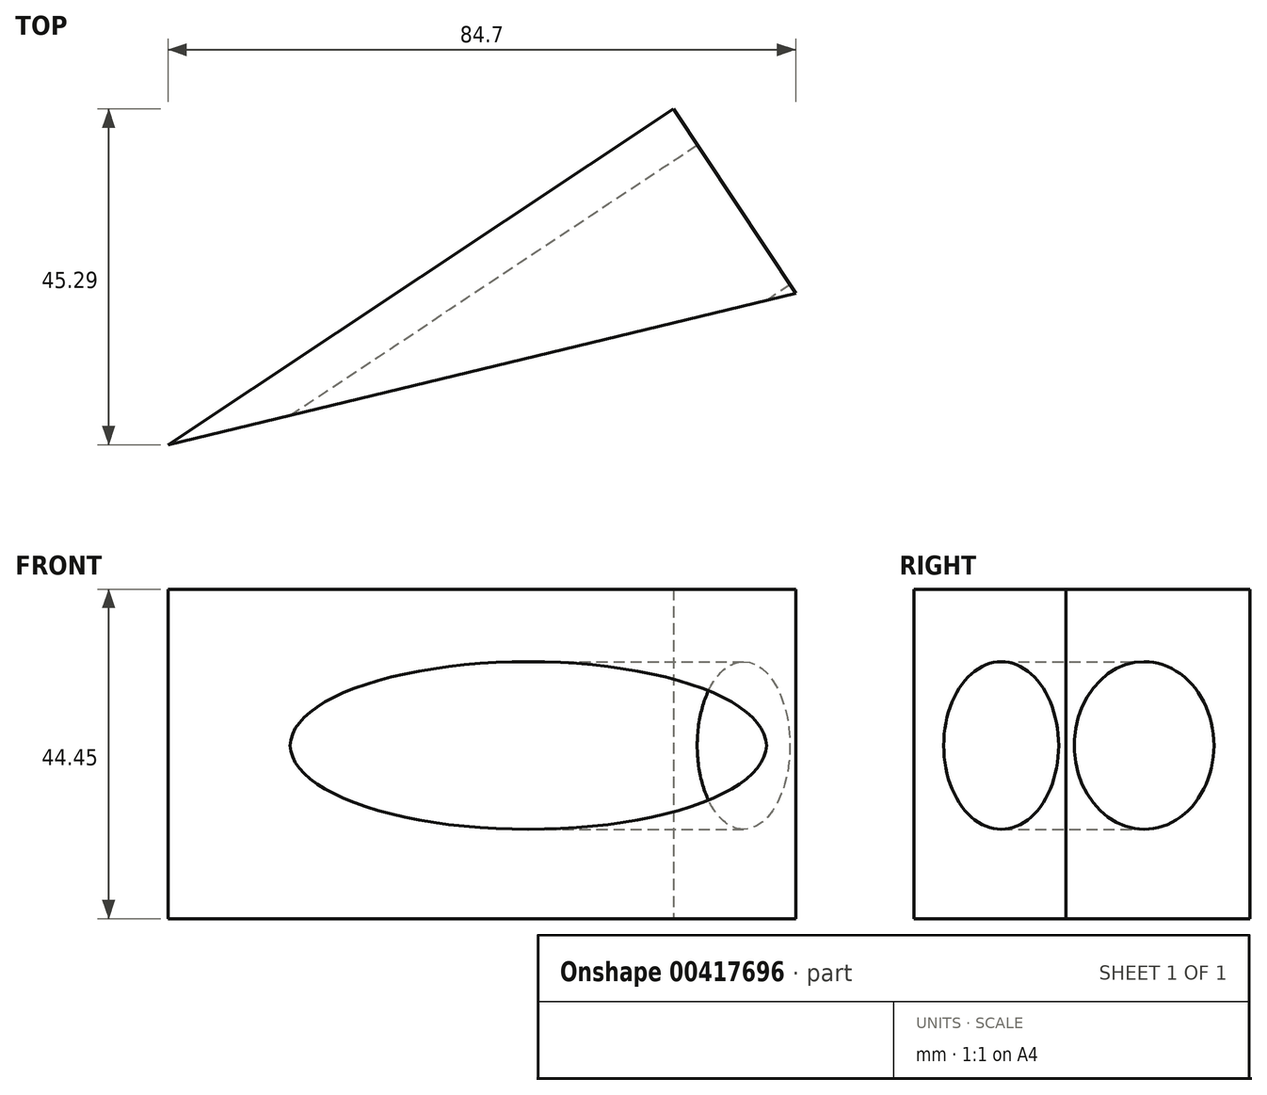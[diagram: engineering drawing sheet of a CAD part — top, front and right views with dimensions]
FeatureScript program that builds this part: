
annotation { "Feature Type Name" : "Feature", "Feature Type Description" : "" }
export const myFeature = defineFeature(function(context is Context, id is Id, definition is map)
    precondition{}
    {
        {
            var Q0;
            Q0=qCreatedBy(makeId("Top.planeOp"),FACE);
            var sketch = newSketch(context, id + "F0", { "sketchPlane" : qUnion([Q0])});
            skLineSegment(sketch, "E0", {"start": v(0, 0) * mm, "end": v(68.2, 45.3) * mm});
            skLineSegment(sketch, "E1", {"start": v(68.2, 45.3) * mm, "end": v(84.7, 20.45) * mm});
            skLineSegment(sketch, "E2", {"start": v(84.7, 20.45) * mm, "end": v(0, 0) * mm});
            skSolve(sketch);
        }
        {
            var Q0;
            Q0 = qSketchRegion(id + "F0", true);
            extrude(context, id + "F1", {"entities" : qUnion([Q0]), "depth" : 44.45 * mm});
        }
        {
            var Q0;
            Q0=makeQuery(id+"F1.opExtrude","SWEPT_FACE",FACE,{"disambiguationData":[OSD([sQuery(id+"F0.wireOp",EDGE,"E1")])]});
            var sketch = newSketch(context, id + "F2", { "sketchPlane" : qUnion([Q0])});
            skCircle(sketch, "E3", {"center": v(-17.12, 23.37) * mm, "radius": 11.31 * mm});
            skSolve(sketch);
        }
        {
            var Q0;
            Q0=makeQuery(id+"F2.imprint","IMPRINT",FACE,{"disambiguationData":[TD([[makeQuery(id+"F2.imprint","IMPRINT",EDGE,{"derivedFrom":sQuery(id+"F2.wireOp",EDGE,"E3")}),1.0]])]});
            extrude(context, id + "F3", {"entities" : qUnion([Q0]), "operationType" : NewBodyOperationType.REMOVE, "endBound" : BoundingType.THROUGH_ALL, "oppositeDirection" : true, "depth" : 25.4 * mm});
        }
    });
